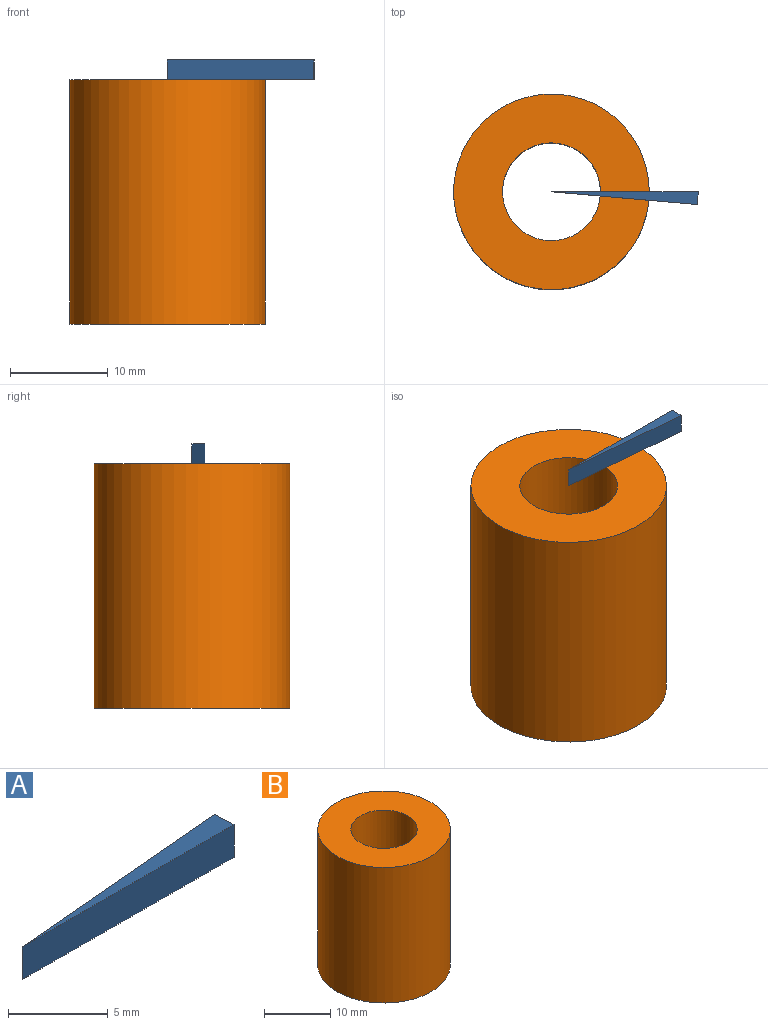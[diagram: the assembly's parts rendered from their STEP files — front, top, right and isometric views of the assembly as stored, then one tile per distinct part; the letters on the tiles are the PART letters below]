
ASSEMBLY  parts=2 mates=1
PART A: 5 faces, bbox 15x1.3x2 mm
  f0: plane 14.94x2mm, normal (-0.09,1,0), area 30mm2, adj f1,f2,f3,f4
  f1: plane 15x2mm, normal (0,-1,0), area 30mm2, adj f0,f2,f3,f4
  f2: plane 2x1.31mm, normal (1,0.04,0), area 2.6mm2, adj f0,f1,f3,f4
  f3: plane 15x1.31mm, normal (0,0,1), area 9.8mm2, adj f0,f1,f2
  f4: plane 15x1.31mm, normal (0,0,-1), area 9.8mm2, adj f0,f1,f2
PART B: 4 faces, bbox 20x20x25 mm
  f0: cylinder r=5mm len=25mm, axis (0,0,-1), area 785.4mm2, adj f2,f3
  f1: cylinder r=10mm len=25mm, axis (0,0,-1), area 1570.8mm2, adj f2,f3
  f2: plane 20x20mm, normal (0,0,1), area 235.6mm2, adj f0,f1
  f3: plane 20x20mm, normal (0,0,-1), area 235.6mm2, adj f0,f1
PLACE A rot(axis=(1,0,0),180deg) t=(0,0,52)mm
PLACE B at identity fixed
MATE ball B.f0 <-> A.f3  axis (0,0,1) through (0,0,25)mm
